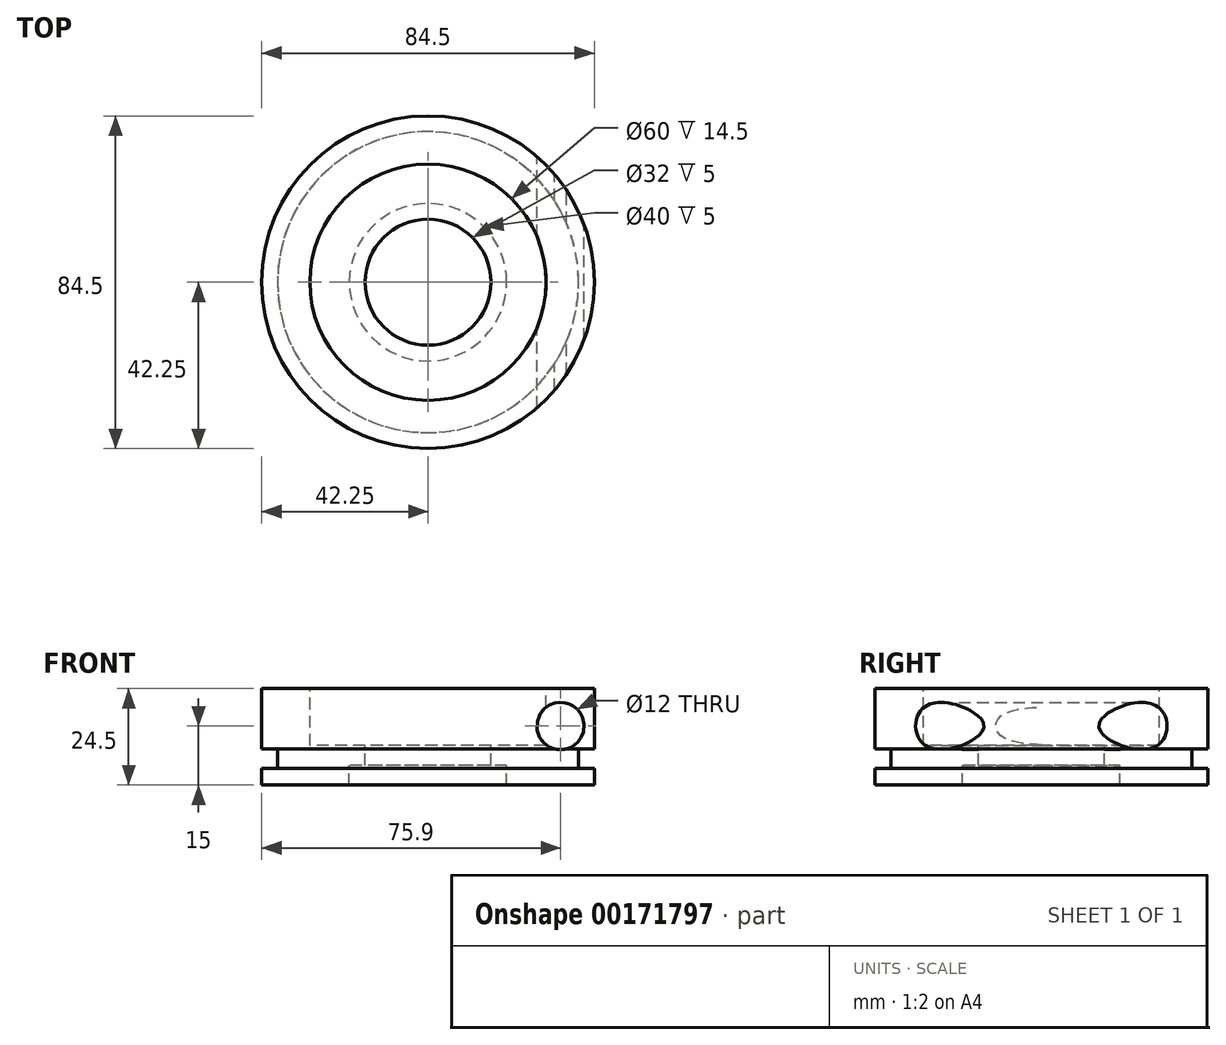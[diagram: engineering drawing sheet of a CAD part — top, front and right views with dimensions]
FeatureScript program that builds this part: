
annotation { "Feature Type Name" : "Feature", "Feature Type Description" : "" }
export const myFeature = defineFeature(function(context is Context, id is Id, definition is map)
    precondition{}
    {
        {
            var Q0;
            Q0=qCreatedBy(makeId("Front.planeOp"),FACE);
            var sketch = newSketch(context, id + "F0", { "sketchPlane" : qUnion([Q0])});
            skLineSegment(sketch, "E0", {"start": v(0, 80.42) * mm, "end": v(0, -77.76) * mm, "construction": true});
            skLineSegment(sketch, "E1", {"start": v(20, 0) * mm, "end": v(42.25, 0) * mm});
            skLineSegment(sketch, "E2", {"start": v(42.25, 0) * mm, "end": v(42.25, 4.2) * mm});
            skLineSegment(sketch, "E3", {"start": v(42.25, 24.5) * mm, "end": v(30, 24.5) * mm});
            skLineSegment(sketch, "E4", {"start": v(30, 24.5) * mm, "end": v(30, 10) * mm});
            skLineSegment(sketch, "E5", {"start": v(30, 10) * mm, "end": v(16, 10) * mm});
            skLineSegment(sketch, "E6", {"start": v(16, 10) * mm, "end": v(16, 5) * mm});
            skLineSegment(sketch, "E7", {"start": v(16, 5) * mm, "end": v(20, 5) * mm});
            skLineSegment(sketch, "E8", {"start": v(20, 5) * mm, "end": v(20, 0) * mm});
            skLineSegment(sketch, "E9", {"start": v(42.25, 4.2) * mm, "end": v(38.25, 4.2) * mm});
            skLineSegment(sketch, "E10", {"start": v(38.25, 4.2) * mm, "end": v(38.25, 9.2) * mm});
            skLineSegment(sketch, "E11", {"start": v(38.25, 9.2) * mm, "end": v(42.25, 9.2) * mm});
            skLineSegment(sketch, "E12.trimOffspring", {"start": v(42.25, 9.2) * mm, "end": v(42.25, 24.5) * mm});
            skSolve(sketch);
        }
        {
            var Q0;
            Q0=makeQuery(id+"F0.imprint","IMPRINT",FACE,{"disambiguationData":[TD([[makeQuery(id+"F0.imprint","IMPRINT",EDGE,{"derivedFrom":sQuery(id+"F0.wireOp",EDGE,"E1")}),1.0]])]});
            var Q1;
            Q1=sQuery(id+"F0.wireOp",EDGE,"E0");
            revolve(context, id + "F1", {"entities" : qUnion([Q0]), "axis" : qUnion([Q1]), "revolveType" : RevolveType.FULL});
        }
        {
            var Q0;
            Q0=qCreatedBy(makeId("Front.planeOp"),FACE);
            var sketch = newSketch(context, id + "F2", { "sketchPlane" : qUnion([Q0])});
            skCircle(sketch, "E13", {"center": v(33.65, 15) * mm, "radius": 6 * mm});
            skSolve(sketch);
        }
        {
            var Q0;
            Q0=makeQuery(id+"F2.imprint","IMPRINT",FACE,{"disambiguationData":[TD([[makeQuery(id+"F2.imprint","IMPRINT",EDGE,{"derivedFrom":sQuery(id+"F2.wireOp",EDGE,"E13")}),1.0]])]});
            var Q1;
            Q1=sQuery(id+"F2.wireOp",EDGE,"E13");
            extrude(context, id + "F3", {"entities" : qUnion([Q0]), "surfaceEntities" : qUnion([Q1]), "depth" : 100 * mm, "symmetric" : true});
        }
        {
            var Q0;
            Q0=makeQuery(id+"F3.opExtrude","SWEPT_BODY",BODY,{"disambiguationData":[OSD([sQuery(id+"F2.wireOp",EDGE,"E13")])]});
            var Q1;
            Q1=makeQuery(id+"F1.opRevolve","SWEPT_BODY",BODY,{"disambiguationData":[OSD([sQuery(id+"F0.wireOp",EDGE,"E1"),sQuery(id+"F0.wireOp",EDGE,"E2"),sQuery(id+"F0.wireOp",EDGE,"E3"),sQuery(id+"F0.wireOp",EDGE,"E4"),sQuery(id+"F0.wireOp",EDGE,"E5"),sQuery(id+"F0.wireOp",EDGE,"E6"),sQuery(id+"F0.wireOp",EDGE,"E7"),sQuery(id+"F0.wireOp",EDGE,"E8"),sQuery(id+"F0.wireOp",EDGE,"E9"),sQuery(id+"F0.wireOp",EDGE,"E10"),sQuery(id+"F0.wireOp",EDGE,"E11"),sQuery(id+"F0.wireOp",EDGE,"E12.trimOffspring")])]});
            booleanBodies(context, id + "F4", {"operationType" : BooleanOperationType.SUBTRACTION, "tools" : qUnion([Q0]), "targets" : qUnion([Q1])});
        }
    });
